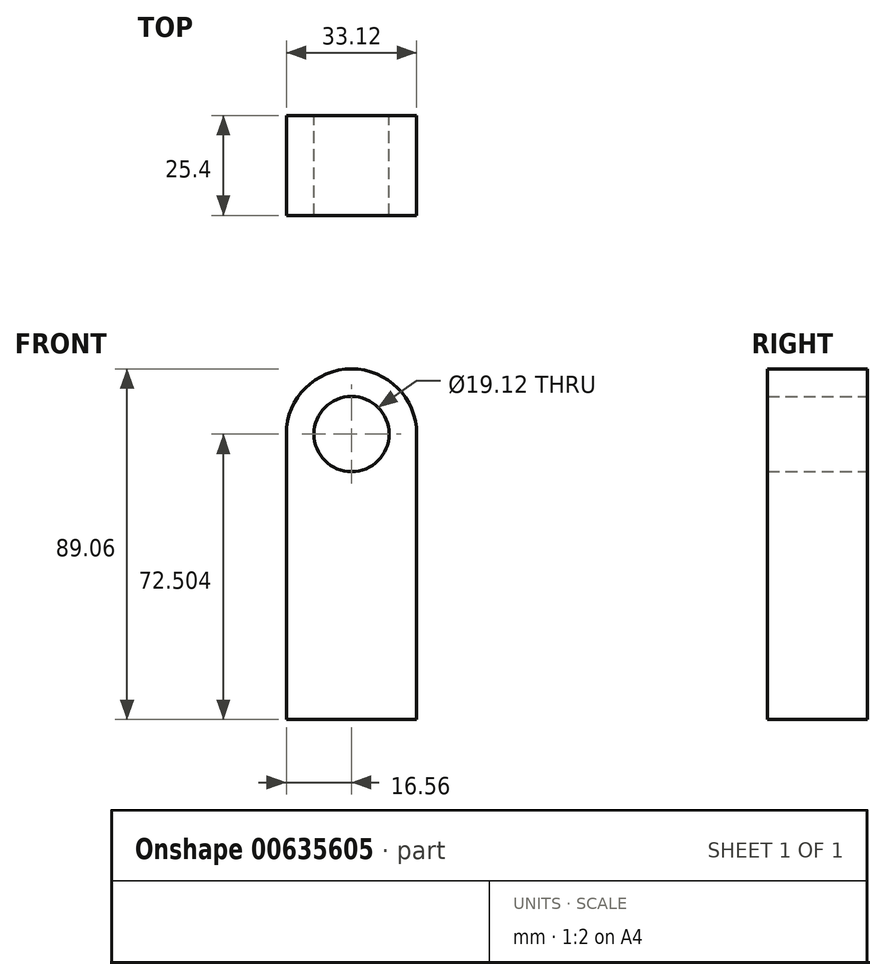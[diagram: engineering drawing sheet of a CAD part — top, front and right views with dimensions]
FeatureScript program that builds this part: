
annotation { "Feature Type Name" : "Feature", "Feature Type Description" : "" }
export const myFeature = defineFeature(function(context is Context, id is Id, definition is map)
    precondition{}
    {
        {
            var Q0;
            Q0=qCreatedBy(makeId("Front.planeOp"),FACE);
            var sketch = newSketch(context, id + "F0", { "sketchPlane" : qUnion([Q0])});
            skLineSegment(sketch, "E0.top", {"start": v(16.56, -36.25) * mm, "end": v(-16.56, -36.25) * mm});
            skLineSegment(sketch, "E0.left", {"start": v(16.56, 36.25) * mm, "end": v(16.56, -36.25) * mm});
            skLineSegment(sketch, "E0.right", {"start": v(-16.56, 36.25) * mm, "end": v(-16.56, -36.25) * mm});
            skPoint(sketch, "E0.middle", {"position": v(0, 0) * mm});
            skArc(sketch, "E1", {"start": v(16.56, 36.25) * mm, "mid": v(0, 52.81) * mm, "end": v(-16.56, 36.25) * mm});
            skCircle(sketch, "E2", {"center": v(0, 36.25) * mm, "radius": 9.56 * mm});
            skSolve(sketch);
        }
        {
            var Q0;
            Q0 = qSketchRegion(id + "F0", true);
            extrude(context, id + "F1", {"entities" : qUnion([Q0]), "depth" : 25.4 * mm, "offsetDistance" : 25.4 * mm});
        }
    });
